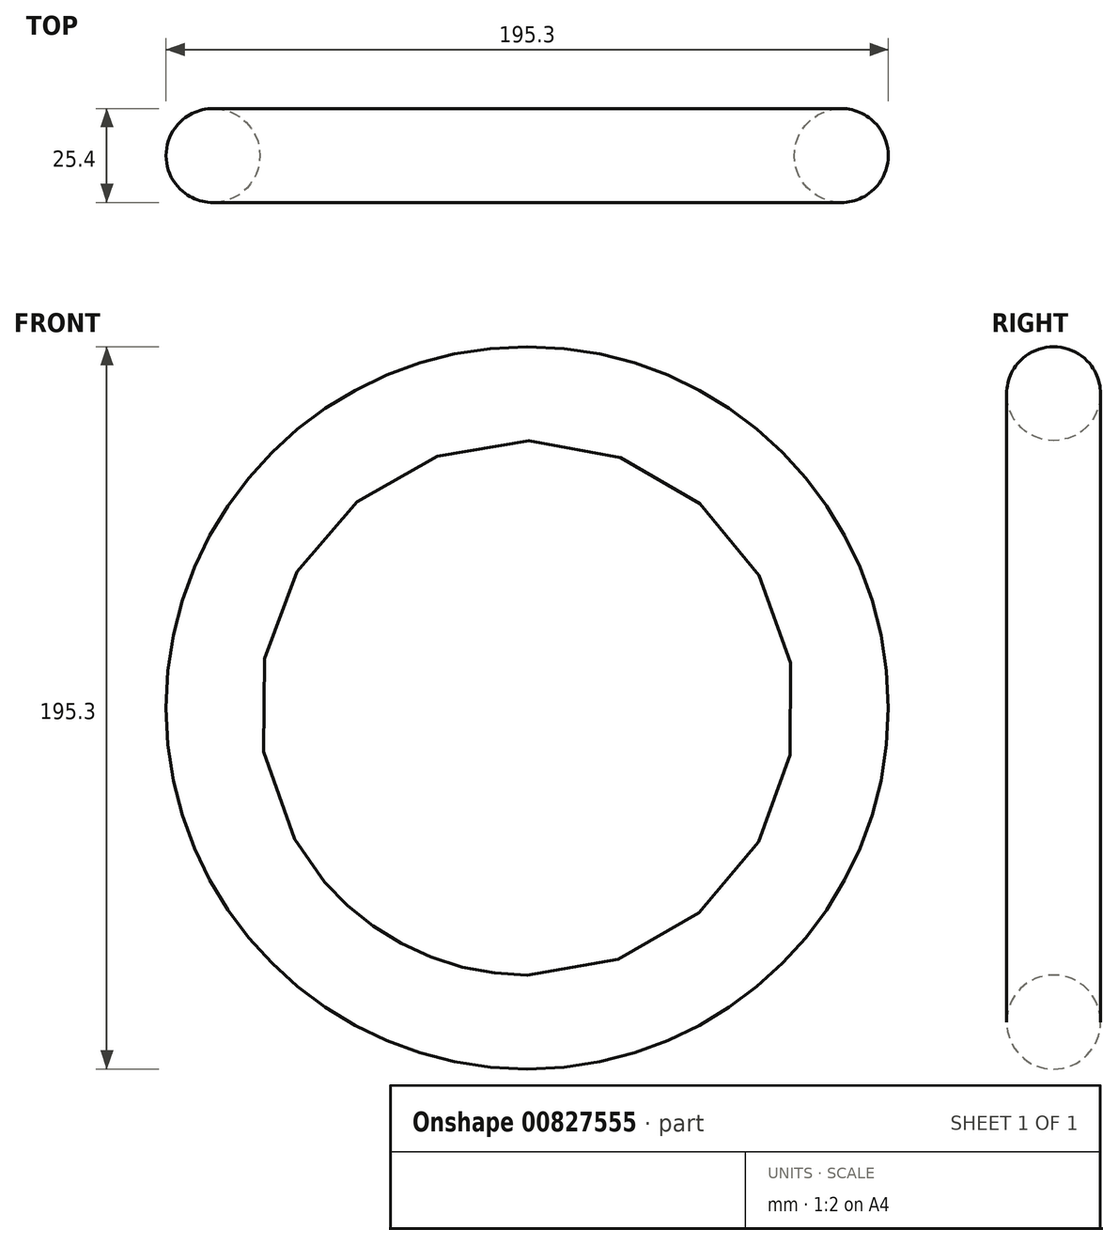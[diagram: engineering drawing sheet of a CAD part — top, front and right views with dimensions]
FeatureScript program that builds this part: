
annotation { "Feature Type Name" : "Feature", "Feature Type Description" : "" }
export const myFeature = defineFeature(function(context is Context, id is Id, definition is map)
    precondition{}
    {
        {
            var Q0;
            Q0=qCreatedBy(makeId("Top.planeOp"),FACE);
            var sketch = newSketch(context, id + "F0", { "sketchPlane" : qUnion([Q0])});
            skCircle(sketch, "E0", {"center": v(-84.95, 9.28) * mm, "radius": 12.7 * mm});
            skSolve(sketch);
        }
        {
            var Q0;
            Q0=qCreatedBy(makeId("Top.planeOp"),FACE);
            var sketch = newSketch(context, id + "F1", { "sketchPlane" : qUnion([Q0])});
            skLineSegment(sketch, "E1", {"start": v(0, -81.4) * mm, "end": v(0, 78.07) * mm});
            skSolve(sketch);
        }
        {
            var Q0;
            Q0=makeQuery(id+"F0.imprint","IMPRINT",FACE,{"disambiguationData":[TD([[makeQuery(id+"F0.imprint","IMPRINT",EDGE,{"derivedFrom":sQuery(id+"F0.wireOp",EDGE,"E0")}),1.0]])]});
            var Q1;
            Q1=sQuery(id+"F1.wireOp",EDGE,"E1");
            revolve(context, id + "F2", {"surfaceOperationType" : NewSurfaceOperationType.NEW, "entities" : qUnion([Q0]), "axis" : qUnion([Q1]), "revolveType" : RevolveType.FULL});
        }
    });
